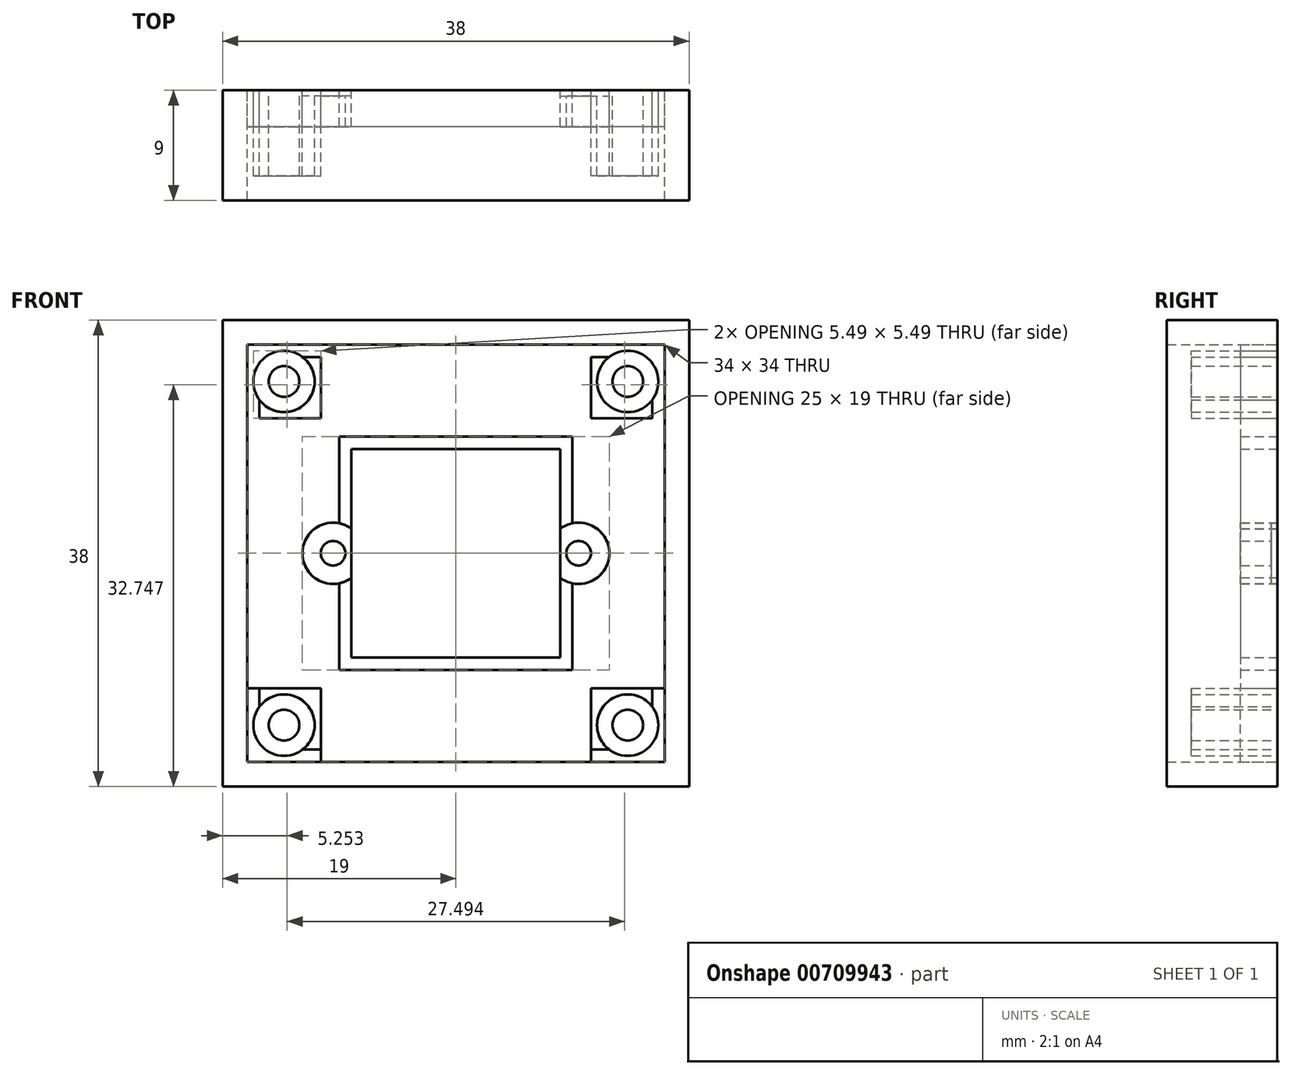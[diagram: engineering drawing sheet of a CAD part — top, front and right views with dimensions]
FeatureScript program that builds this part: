
annotation { "Feature Type Name" : "Feature", "Feature Type Description" : "" }
export const myFeature = defineFeature(function(context is Context, id is Id, definition is map)
    precondition{}
    {
        {
            var Q0;
            Q0=qCreatedBy(makeId("Front.planeOp"),FACE);
            var sketch = newSketch(context, id + "F0", { "sketchPlane" : qUnion([Q0])});
            skLineSegment(sketch, "E0.left", {"start": v(16, 12.5) * mm, "end": v(16, -12.5) * mm});
            skPoint(sketch, "E0.middle", {"position": v(0, 0) * mm});
            skLineSegment(sketch, "E1.bottom", {"start": v(8.5, 8.5) * mm, "end": v(-8.5, 8.5) * mm});
            skLineSegment(sketch, "E1.top", {"start": v(8.5, -8.5) * mm, "end": v(-8.5, -8.5) * mm});
            skLineSegment(sketch, "E1.left", {"start": v(8.5, 8.5) * mm, "end": v(8.5, -8.5) * mm});
            skLineSegment(sketch, "E1.right", {"start": v(-8.5, 8.5) * mm, "end": v(-8.5, -8.5) * mm});
            skCircle(sketch, "E2", {"center": v(-14, 14) * mm, "radius": 1.25 * mm});
            skCircle(sketch, "E3", {"center": v(14, -14) * mm, "radius": 1.25 * mm});
            skCircle(sketch, "E4", {"center": v(14, 14) * mm, "radius": 1.25 * mm});
            skCircle(sketch, "E5", {"center": v(-14, -14) * mm, "radius": 1.25 * mm});
            skCircle(sketch, "E6", {"center": v(0, 0) * mm, "radius": 8.5 * mm});
            skCircle(sketch, "E7", {"center": v(-10, 0) * mm, "radius": 1 * mm});
            skCircle(sketch, "E8", {"center": v(10, 0) * mm, "radius": 1 * mm});
            skPoint(sketch, "E9.left.start.orphan", {"position": v(10, -1.28) * mm});
            skPoint(sketch, "E10.trimOffspring.end.orphan", {"position": v(10, 1.28) * mm});
            skPoint(sketch, "E11.trimOffspring.end.orphan", {"position": v(-10, 1.28) * mm});
            skPoint(sketch, "E9.right.start.orphan", {"position": v(-10, -1.28) * mm});
            skLineSegment(sketch, "E12.left", {"start": v(16, 12.5) * mm, "end": v(16, 10.2) * mm});
            skLineSegment(sketch, "E12.right", {"start": v(10, 16) * mm, "end": v(10, 10.2) * mm});
            skLineSegment(sketch, "E13.bottom", {"start": v(10, 16) * mm, "end": v(0, 16) * mm});
            skLineSegment(sketch, "E13.top", {"start": v(10, 10) * mm, "end": v(0, 10) * mm});
            skLineSegment(sketch, "E13.left", {"start": v(10, 16) * mm, "end": v(10, 10) * mm});
            skLineSegment(sketch, "E13.right", {"start": v(0, 16) * mm, "end": v(0, 10) * mm});
            skLineSegment(sketch, "E14.top", {"start": v(-16, 10) * mm, "end": v(-10, 10) * mm});
            skLineSegment(sketch, "E15.top", {"start": v(-16, 4) * mm, "end": v(-10, 4) * mm});
            skLineSegment(sketch, "E15.left", {"start": v(-16, 10) * mm, "end": v(-16, 4) * mm});
            skLineSegment(sketch, "E15.right", {"start": v(-10, 10) * mm, "end": v(-10, 4) * mm});
            skLineSegment(sketch, "E16.bottom", {"start": v(17, 17) * mm, "end": v(-17, 17) * mm});
            skLineSegment(sketch, "E16.top", {"start": v(17, -17) * mm, "end": v(-17, -17) * mm});
            skLineSegment(sketch, "E16.left", {"start": v(17, 17) * mm, "end": v(17, -17) * mm});
            skLineSegment(sketch, "E16.right", {"start": v(-17, 17) * mm, "end": v(-17, -17) * mm});
            skLineSegment(sketch, "E17.bottom", {"start": v(19, 19) * mm, "end": v(-19, 19) * mm});
            skLineSegment(sketch, "E17.top", {"start": v(19, -19) * mm, "end": v(-19, -19) * mm});
            skLineSegment(sketch, "E17.left", {"start": v(19, 19) * mm, "end": v(19, -19) * mm});
            skLineSegment(sketch, "E17.right", {"start": v(-19, 19) * mm, "end": v(-19, -19) * mm});
            skLineSegment(sketch, "E18.bottom", {"start": v(9.5, 9.5) * mm, "end": v(-9.5, 9.5) * mm});
            skLineSegment(sketch, "E18.top", {"start": v(9.5, -9.5) * mm, "end": v(-9.5, -9.5) * mm});
            skLineSegment(sketch, "E18.left", {"start": v(9.5, 9.5) * mm, "end": v(9.5, 2.45) * mm});
            skLineSegment(sketch, "E18.right", {"start": v(-9.5, 9.5) * mm, "end": v(-9.5, 2.45) * mm});
            skCircle(sketch, "E19", {"center": v(-14, 14) * mm, "radius": 2.5 * mm});
            skCircle(sketch, "E20", {"center": v(14, 14) * mm, "radius": 2.5 * mm});
            skCircle(sketch, "E21", {"center": v(-14, -14) * mm, "radius": 2.5 * mm});
            skCircle(sketch, "E22", {"center": v(14, -14) * mm, "radius": 2.5 * mm});
            skLineSegment(sketch, "E23.trimOffspring", {"start": v(-16, 12.5) * mm, "end": v(-16, 10) * mm});
            skLineSegment(sketch, "E24.trimOffspring", {"start": v(-16, 12.5) * mm, "end": v(-16, -12.5) * mm});
            skLineSegment(sketch, "E25.trimOffspring", {"start": v(-12.5, 16) * mm, "end": v(-10, 16) * mm});
            skPoint(sketch, "E26.trimOffspring.end.orphan", {"position": v(-16, 16) * mm});
            skLineSegment(sketch, "E27.trimOffspring", {"start": v(12.5, 16) * mm, "end": v(-12.5, 16) * mm});
            skLineSegment(sketch, "E28.trimOffspring", {"start": v(12.5, 16) * mm, "end": v(10, 16) * mm});
            skPoint(sketch, "E29.orphan", {"position": v(16, 16.78) * mm});
            skPoint(sketch, "E30.orphan", {"position": v(-16, -16.78) * mm});
            skLineSegment(sketch, "E31.trimOffspring", {"start": v(12.5, -16) * mm, "end": v(-12.5, -16) * mm});
            skPoint(sketch, "E32.trimOffspring.end.orphan", {"position": v(16, -16) * mm});
            skArc(sketch, "E33", {"start": v(-9.5, 2.45) * mm, "mid": v(-12.5, 0) * mm, "end": v(-9.5, -2.45) * mm});
            skArc(sketch, "E34", {"start": v(9.5, -2.45) * mm, "mid": v(12.5, 0) * mm, "end": v(9.5, 2.45) * mm});
            skLineSegment(sketch, "E35.trimOffspring", {"start": v(-9.5, -2.45) * mm, "end": v(-9.5, -9.5) * mm});
            skLineSegment(sketch, "E36.trimOffspring", {"start": v(9.5, -2.45) * mm, "end": v(9.5, -9.5) * mm});
            skArc(sketch, "E37", {"start": v(8.5, -2) * mm, "mid": v(12.5, 0) * mm, "end": v(8.5, 2) * mm});
            skArc(sketch, "E38", {"start": v(-8.5, 2) * mm, "mid": v(-12.5, 0) * mm, "end": v(-8.5, -2) * mm});
            skPoint(sketch, "E39", {"position": v(8.5, 2) * mm});
            skPoint(sketch, "E40", {"position": v(8.5, -2) * mm});
            skPoint(sketch, "E41", {"position": v(-8.5, 2) * mm});
            skPoint(sketch, "E42", {"position": v(-8.5, -2) * mm});
            skLineSegment(sketch, "E43.bottom", {"start": v(-17, 17) * mm, "end": v(-11, 17) * mm});
            skLineSegment(sketch, "E43.top", {"start": v(-17, 11) * mm, "end": v(-11, 11) * mm});
            skLineSegment(sketch, "E43.left", {"start": v(-17, 17) * mm, "end": v(-17, 11) * mm});
            skLineSegment(sketch, "E43.right", {"start": v(-11, 17) * mm, "end": v(-11, 11) * mm});
            skLineSegment(sketch, "E44.bottom", {"start": v(17, 17) * mm, "end": v(11, 17) * mm});
            skLineSegment(sketch, "E44.top", {"start": v(17, 11) * mm, "end": v(11, 11) * mm});
            skLineSegment(sketch, "E44.left", {"start": v(17, 17) * mm, "end": v(17, 11) * mm});
            skLineSegment(sketch, "E44.right", {"start": v(11, 17) * mm, "end": v(11, 11) * mm});
            skLineSegment(sketch, "E45.bottom", {"start": v(17, -17) * mm, "end": v(11, -17) * mm});
            skLineSegment(sketch, "E45.top", {"start": v(17, -11) * mm, "end": v(11, -11) * mm});
            skLineSegment(sketch, "E45.left", {"start": v(17, -17) * mm, "end": v(17, -11) * mm});
            skLineSegment(sketch, "E45.right", {"start": v(11, -17) * mm, "end": v(11, -11) * mm});
            skLineSegment(sketch, "E46.bottom", {"start": v(-17, -17) * mm, "end": v(-11, -17) * mm});
            skLineSegment(sketch, "E46.top", {"start": v(-17, -11) * mm, "end": v(-11, -11) * mm});
            skLineSegment(sketch, "E46.left", {"start": v(-17, -17) * mm, "end": v(-17, -11) * mm});
            skLineSegment(sketch, "E46.right", {"start": v(-11, -17) * mm, "end": v(-11, -11) * mm});
            skSolve(sketch);
        }
        {
            var Q0;
            Q0=makeQuery(id+"F0.imprint","IMPRINT",FACE,{"disambiguationData":[TD([[makeQuery(id+"F0.imprint","IMPRINT",EDGE,{"derivedFrom":sQuery(id+"F0.wireOp",EDGE,"E2")}),-1.0]])]});
            var Q1;
            Q1=makeQuery(id+"F0.imprint","IMPRINT",FACE,{"disambiguationData":[TD([[makeQuery(id+"F0.imprint","IMPRINT",EDGE,{"derivedFrom":sQuery(id+"F0.wireOp",EDGE,"E4")}),-1.0]])]});
            var Q2;
            Q2=makeQuery(id+"F0.imprint","IMPRINT",FACE,{"disambiguationData":[TD([[makeQuery(id+"F0.imprint","IMPRINT",EDGE,{"derivedFrom":sQuery(id+"F0.wireOp",EDGE,"E5")}),-1.0]])]});
            var Q3;
            Q3=makeQuery(id+"F0.imprint","IMPRINT",FACE,{"disambiguationData":[TD([[makeQuery(id+"F0.imprint","IMPRINT",EDGE,{"derivedFrom":sQuery(id+"F0.wireOp",EDGE,"E3")}),-1.0]])]});
            extrude(context, id + "F1", {"entities" : qUnion([Q0, Q1, Q2, Q3]), "depth" : 7 * mm, "offsetDistance" : 25 * mm});
        }
        {
            var Q0;
            Q0=makeQuery(id+"F0.imprint","IMPRINT",FACE,{"disambiguationData":[TD([[makeQuery(id+"F0.imprint","IMPRINT",EDGE,{"derivedFrom":sQuery(id+"F0.wireOp",EDGE,"E7")}),-1.0]])]});
            var Q1;
            Q1=makeQuery(id+"F0.imprint","IMPRINT",FACE,{"disambiguationData":[TD([[makeQuery(id+"F0.imprint","IMPRINT",EDGE,{"derivedFrom":sQuery(id+"F0.wireOp",EDGE,"E8")}),-1.0]])]});
            extrude(context, id + "F2", {"entities" : qUnion([Q0, Q1]), "depth" : 3 * mm, "offsetDistance" : 25 * mm});
        }
        {
            var Q0;
            Q0=makeQuery(id+"F0.imprint","IMPRINT",FACE,{"disambiguationData":[TD([[makeQuery(id+"F0.imprint","IMPRINT",EDGE,{"derivedFrom":sQuery(id+"F0.wireOp",EDGE,"E18.bottom")}),1.0]])]});
            extrude(context, id + "F3", {"entities" : qUnion([Q0]), "depth" : 3 * mm, "offsetDistance" : 25 * mm});
        }
        {
            var Q0;
            {var subQ0=sQuery(id+"F0.wireOp",EDGE,"E24.trimOffspring");var subQ1=sQuery(id+"F0.wireOp",EDGE,"E19");var subQ2=makeQuery(id+"F0.imprint","INTERSECT",VERTEX,{"derivedFrom":[subQ1,subQ0]});Q0=makeQuery(id+"F0.imprint","IMPRINT",FACE,{"disambiguationData":[TD([[makeQuery(id+"F0.imprint","IMPRINT",EDGE,{"disambiguationData":[TD([[subQ2,-1.0]])],"derivedFrom":subQ1}),-1.0]])]});}
            var Q1;
            {var subQ0=sQuery(id+"F0.wireOp",EDGE,"E43.bottom");Q1=makeQuery(id+"F0.imprint","IMPRINT",FACE,{"disambiguationData":[TD([[makeQuery(id+"F0.imprint","IMPRINT",EDGE,{"derivedFrom":subQ0}),-1.0]])]});}
            var Q2;
            {var subQ0=sQuery(id+"F0.wireOp",EDGE,"E44.bottom");Q2=makeQuery(id+"F0.imprint","IMPRINT",FACE,{"disambiguationData":[TD([[makeQuery(id+"F0.imprint","IMPRINT",EDGE,{"derivedFrom":subQ0}),1.0]])]});}
            var Q3;
            {var subQ3=sQuery(id+"F0.wireOp",EDGE,"E12.left");var subQ6=sQuery(id+"F0.wireOp",EDGE,"E20");var subQ9=makeQuery(id+"F0.imprint","INTERSECT",VERTEX,{"derivedFrom":[subQ3,subQ6]});Q3=makeQuery(id+"F0.imprint","IMPRINT",FACE,{"disambiguationData":[TD([[makeQuery(id+"F0.imprint","IMPRINT",EDGE,{"disambiguationData":[TD([[subQ9,-1.0]])],"derivedFrom":subQ3}),-1.0]])]});}
            var Q4;
            {var subQ5=sQuery(id+"F0.wireOp",EDGE,"E45.bottom");Q4=makeQuery(id+"F0.imprint","IMPRINT",FACE,{"disambiguationData":[TD([[makeQuery(id+"F0.imprint","IMPRINT",EDGE,{"derivedFrom":subQ5}),-1.0]])]});}
            var Q5;
            {var subQ3=sQuery(id+"F0.wireOp",EDGE,"E24.trimOffspring");var subQ5=sQuery(id+"F0.wireOp",EDGE,"E21");var subQ6=makeQuery(id+"F0.imprint","INTERSECT",VERTEX,{"derivedFrom":[subQ5,subQ3]});Q5=makeQuery(id+"F0.imprint","IMPRINT",FACE,{"disambiguationData":[TD([[makeQuery(id+"F0.imprint","IMPRINT",EDGE,{"disambiguationData":[TD([[subQ6,1.0]])],"derivedFrom":subQ5}),-1.0]])]});}
            var Q6;
            {var subQ5=sQuery(id+"F0.wireOp",EDGE,"E46.bottom");Q6=makeQuery(id+"F0.imprint","IMPRINT",FACE,{"disambiguationData":[TD([[makeQuery(id+"F0.imprint","IMPRINT",EDGE,{"derivedFrom":subQ5}),1.0]])]});}
            var Q7;
            {var subQ3=sQuery(id+"F0.wireOp",EDGE,"E0.left");var subQ6=sQuery(id+"F0.wireOp",EDGE,"E22");var subQ9=makeQuery(id+"F0.imprint","INTERSECT",VERTEX,{"derivedFrom":[subQ3,subQ6]});Q7=makeQuery(id+"F0.imprint","IMPRINT",FACE,{"disambiguationData":[TD([[makeQuery(id+"F0.imprint","IMPRINT",EDGE,{"disambiguationData":[TD([[subQ9,1.0]])],"derivedFrom":subQ3}),-1.0]])]});}
            extrude(context, id + "F4", {"entities" : qUnion([Q0, Q1, Q2, Q3, Q4, Q5, Q6, Q7]), "depth" : 7 * mm, "offsetDistance" : 25 * mm});
        }
        {
            var Q0;
            {var subQ7=sQuery(id+"F0.wireOp",EDGE,"E16.bottom");Q0=makeQuery(id+"F0.imprint","IMPRINT",FACE,{"disambiguationData":[TD([[makeQuery(id+"F0.imprint","IMPRINT",EDGE,{"derivedFrom":subQ7}),1.0]])]});}
            var Q1;
            {var subQ24=sQuery(id+"F0.wireOp",EDGE,"E13.top");Q1=makeQuery(id+"F0.imprint","IMPRINT",FACE,{"disambiguationData":[TD([[makeQuery(id+"F0.imprint","IMPRINT",EDGE,{"derivedFrom":subQ24}),1.0]])]});}
            var Q2;
            {var subQ2=sQuery(id+"F0.wireOp",EDGE,"E13.top");Q2=makeQuery(id+"F0.imprint","IMPRINT",FACE,{"disambiguationData":[TD([[makeQuery(id+"F0.imprint","IMPRINT",EDGE,{"derivedFrom":subQ2}),-1.0]])]});}
            var Q3;
            {var subQ0=sQuery(id+"F0.wireOp",EDGE,"E14.top");Q3=makeQuery(id+"F0.imprint","IMPRINT",FACE,{"disambiguationData":[TD([[makeQuery(id+"F0.imprint","IMPRINT",EDGE,{"derivedFrom":subQ0}),-1.0]])]});}
            var Q4;
            {var subQ7=sQuery(id+"F0.wireOp",EDGE,"E16.right");Q4=makeQuery(id+"F0.imprint","IMPRINT",FACE,{"disambiguationData":[TD([[makeQuery(id+"F0.imprint","IMPRINT",EDGE,{"derivedFrom":subQ7}),1.0]])]});}
            var Q5;
            {var subQ0=sQuery(id+"F0.wireOp",EDGE,"E16.top");Q5=makeQuery(id+"F0.imprint","IMPRINT",FACE,{"disambiguationData":[TD([[makeQuery(id+"F0.imprint","IMPRINT",EDGE,{"derivedFrom":subQ0}),-1.0]])]});}
            var Q6;
            {var subQ1=sQuery(id+"F0.wireOp",EDGE,"E16.left");Q6=makeQuery(id+"F0.imprint","IMPRINT",FACE,{"disambiguationData":[TD([[makeQuery(id+"F0.imprint","IMPRINT",EDGE,{"derivedFrom":subQ1}),-1.0]])]});}
            extrude(context, id + "F5", {"entities" : qUnion([Q0, Q1, Q2, Q3, Q4, Q5, Q6]), "depth" : 3 * mm, "offsetDistance" : 25 * mm});
        }
        {
            var Q0;
            Q0=makeQuery(id+"F0.imprint","IMPRINT",FACE,{"disambiguationData":[TD([[makeQuery(id+"F0.imprint","IMPRINT",EDGE,{"derivedFrom":sQuery(id+"F0.wireOp",EDGE,"E16.bottom")}),-1.0]])]});
            extrude(context, id + "F6", {"entities" : qUnion([Q0]), "depth" : 9 * mm, "offsetDistance" : 25 * mm});
        }
        {
            var Q0;
            Q0=makeQuery(id+"F0.imprint","IMPRINT",FACE,{"disambiguationData":[TD([[makeQuery(id+"F0.imprint","IMPRINT",EDGE,{"derivedFrom":sQuery(id+"F0.wireOp",EDGE,"E7")}),-1.0]])]});
            extrude(context, id + "F7", {"entities" : qUnion([Q0]), "operationType" : NewBodyOperationType.REMOVE, "depth" : .5 * mm, "offsetDistance" : 25 * mm});
        }
        {
            var Q0;
            Q0=makeQuery(id+"F0.imprint","IMPRINT",FACE,{"disambiguationData":[TD([[makeQuery(id+"F0.imprint","IMPRINT",EDGE,{"derivedFrom":sQuery(id+"F0.wireOp",EDGE,"E8")}),-1.0]])]});
            extrude(context, id + "F8", {"entities" : qUnion([Q0]), "operationType" : NewBodyOperationType.REMOVE, "depth" : .5 * mm, "offsetDistance" : 25 * mm});
        }
    });
